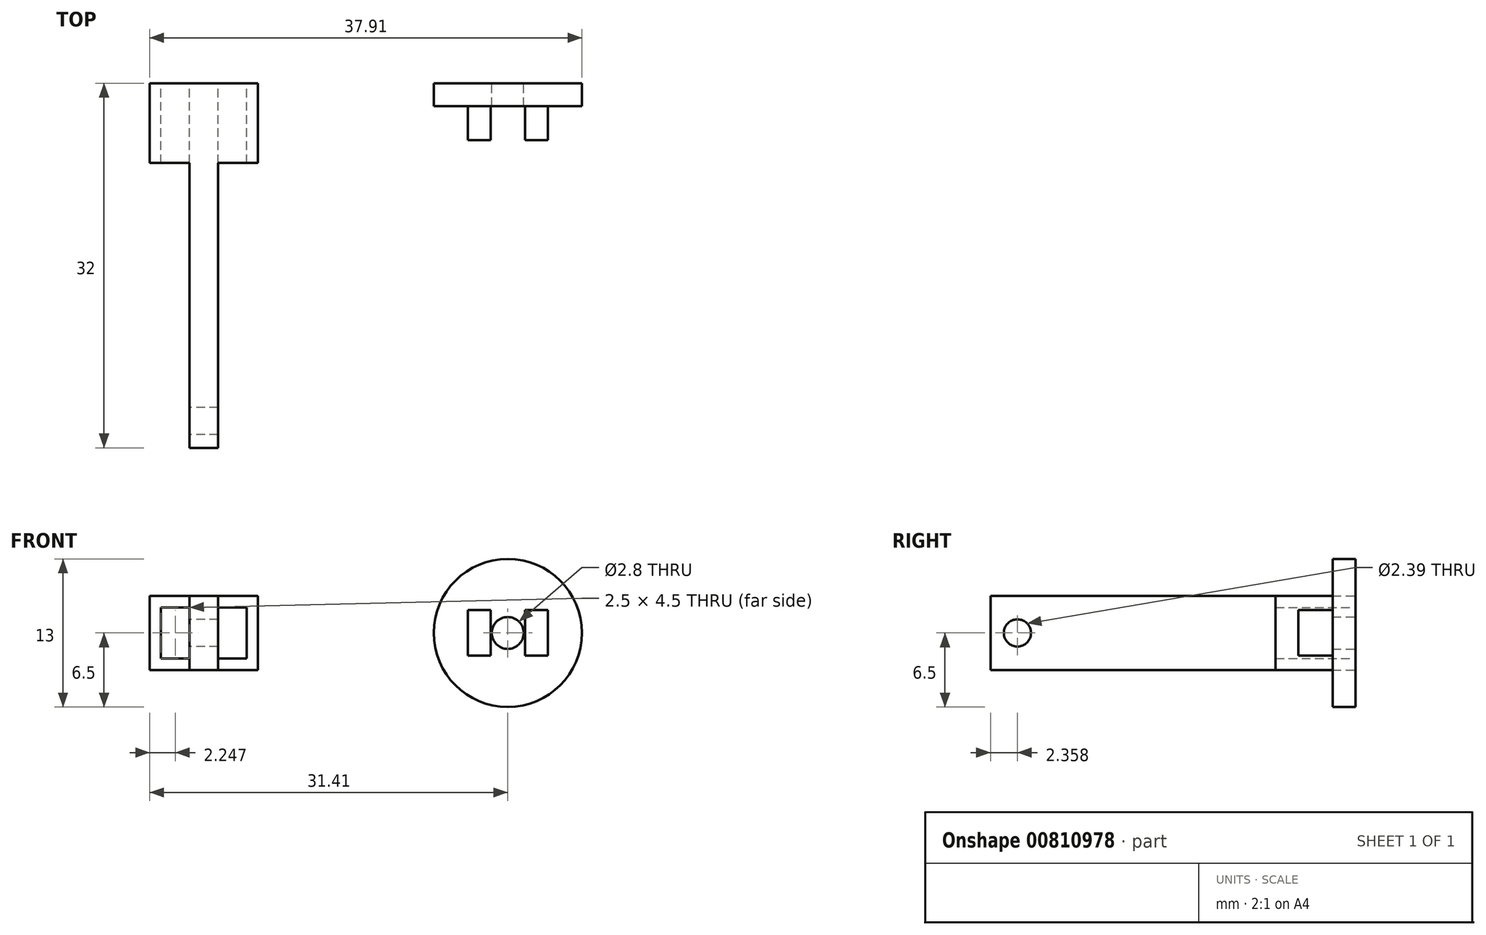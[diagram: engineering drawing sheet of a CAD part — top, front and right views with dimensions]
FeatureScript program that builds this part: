
annotation { "Feature Type Name" : "Feature", "Feature Type Description" : "" }
export const myFeature = defineFeature(function(context is Context, id is Id, definition is map)
    precondition{}
    {
        {
            var Q0;
            Q0=qCreatedBy(makeId("Front.planeOp"),FACE);
            var sketch = newSketch(context, id + "F0", { "sketchPlane" : qUnion([Q0])});
            skCircle(sketch, "E0", {"center": v(0, 0) * mm, "radius": 6.5 * mm});
            skCircle(sketch, "E1", {"center": v(0, 0) * mm, "radius": 1.4 * mm});
            skLineSegment(sketch, "E2.bottom", {"start": v(-3.5, -2) * mm, "end": v(-1.5, -2) * mm});
            skLineSegment(sketch, "E2.top", {"start": v(-3.5, 2) * mm, "end": v(-1.5, 2) * mm});
            skLineSegment(sketch, "E2.left", {"start": v(-3.5, -2) * mm, "end": v(-3.5, 2) * mm});
            skLineSegment(sketch, "E2.right", {"start": v(-1.5, -2) * mm, "end": v(-1.5, 2) * mm});
            skPoint(sketch, "E2.middle", {"position": v(-2.5, 0) * mm});
            skLineSegment(sketch, "E3.bottom", {"start": v(3.5, -2) * mm, "end": v(1.5, -2) * mm});
            skLineSegment(sketch, "E3.top", {"start": v(3.5, 2) * mm, "end": v(1.5, 2) * mm});
            skLineSegment(sketch, "E3.left", {"start": v(3.5, -2) * mm, "end": v(3.5, 2) * mm});
            skLineSegment(sketch, "E3.right", {"start": v(1.5, -2) * mm, "end": v(1.5, 2) * mm});
            skPoint(sketch, "E3.middle", {"position": v(2.5, 0) * mm});
            skLineSegment(sketch, "E4.bottom", {"start": v(-21.91, -3.25) * mm, "end": v(-31.41, -3.25) * mm});
            skLineSegment(sketch, "E4.top", {"start": v(-21.91, 3.25) * mm, "end": v(-31.41, 3.25) * mm});
            skLineSegment(sketch, "E4.left", {"start": v(-21.91, -3.25) * mm, "end": v(-21.91, 3.25) * mm});
            skLineSegment(sketch, "E4.right", {"start": v(-31.41, -3.25) * mm, "end": v(-31.41, 3.25) * mm});
            skPoint(sketch, "E4.middle", {"position": v(-26.66, 0) * mm});
            skLineSegment(sketch, "E5.bottom", {"start": v(-30.41, 2.25) * mm, "end": v(-27.91, 2.25) * mm});
            skLineSegment(sketch, "E5.top", {"start": v(-30.41, -2.25) * mm, "end": v(-27.91, -2.25) * mm});
            skLineSegment(sketch, "E5.left", {"start": v(-30.41, 2.25) * mm, "end": v(-30.41, -2.25) * mm});
            skLineSegment(sketch, "E5.right", {"start": v(-27.91, 2.25) * mm, "end": v(-27.91, -2.25) * mm});
            skPoint(sketch, "E5.middle", {"position": v(-29.16, 0) * mm});
            skLineSegment(sketch, "E6.bottom", {"start": v(-22.91, 2.25) * mm, "end": v(-25.41, 2.25) * mm});
            skLineSegment(sketch, "E6.top", {"start": v(-22.91, -2.25) * mm, "end": v(-25.41, -2.25) * mm});
            skLineSegment(sketch, "E6.left", {"start": v(-22.91, 2.25) * mm, "end": v(-22.91, -2.25) * mm});
            skLineSegment(sketch, "E6.right", {"start": v(-25.41, 2.25) * mm, "end": v(-25.41, -2.25) * mm});
            skPoint(sketch, "E6.middle", {"position": v(-24.16, 0) * mm});
            skPoint(sketch, "E7", {"position": v(-25.41, 0) * mm});
            skSolve(sketch);
        }
        {
            var Q0;
            Q0=makeQuery(id+"F0.imprint","IMPRINT",FACE,{"disambiguationData":[TD([[makeQuery(id+"F0.imprint","IMPRINT",EDGE,{"derivedFrom":sQuery(id+"F0.wireOp",EDGE,"E0")}),1.0]])]});
            extrude(context, id + "F1", {"entities" : qUnion([Q0]), "depth" : 2 * mm, "offsetDistance" : 25 * mm});
        }
        {
            var Q0;
            Q0=makeQuery(id+"F0.imprint","IMPRINT",FACE,{"disambiguationData":[TD([[makeQuery(id+"F0.imprint","IMPRINT",EDGE,{"derivedFrom":sQuery(id+"F0.wireOp",EDGE,"E2.bottom")}),1.0]])]});
            var Q1;
            Q1=makeQuery(id+"F0.imprint","IMPRINT",FACE,{"disambiguationData":[TD([[makeQuery(id+"F0.imprint","IMPRINT",EDGE,{"derivedFrom":sQuery(id+"F0.wireOp",EDGE,"E3.bottom")}),-1.0]])]});
            extrude(context, id + "F2", {"entities" : qUnion([Q0, Q1]), "operationType" : NewBodyOperationType.ADD, "depth" : 5 * mm, "offsetDistance" : 25 * mm});
        }
        {
            var Q0;
            Q0=makeQuery(id+"F0.imprint","IMPRINT",FACE,{"disambiguationData":[TD([[makeQuery(id+"F0.imprint","IMPRINT",EDGE,{"derivedFrom":sQuery(id+"F0.wireOp",EDGE,"E4.bottom")}),-1.0]])]});
            extrude(context, id + "F3", {"entities" : qUnion([Q0]), "depth" : 7 * mm, "offsetDistance" : 25 * mm});
        }
        {
            var Q0;
            Q0=makeQuery(id+"F3.opExtrude","CAP_FACE",FACE,{"disambiguationData":[OSD([sQuery(id+"F0.wireOp",EDGE,"E4.bottom"),sQuery(id+"F0.wireOp",EDGE,"E4.top"),sQuery(id+"F0.wireOp",EDGE,"E4.left"),sQuery(id+"F0.wireOp",EDGE,"E4.right"),sQuery(id+"F0.wireOp",EDGE,"E5.bottom"),sQuery(id+"F0.wireOp",EDGE,"E5.top"),sQuery(id+"F0.wireOp",EDGE,"E5.left"),sQuery(id+"F0.wireOp",EDGE,"E5.right"),sQuery(id+"F0.wireOp",EDGE,"E6.bottom"),sQuery(id+"F0.wireOp",EDGE,"E6.top"),sQuery(id+"F0.wireOp",EDGE,"E6.left"),sQuery(id+"F0.wireOp",EDGE,"E6.right")])],"isStart":false});
            var sketch = newSketch(context, id + "F4", { "sketchPlane" : qUnion([Q0])});
            skLineSegment(sketch, "E8.bottom", {"start": v(-25.41, -3.25) * mm, "end": v(-27.9, -3.25) * mm});
            skLineSegment(sketch, "E8.top", {"start": v(-25.41, 3.25) * mm, "end": v(-27.9, 3.25) * mm});
            skLineSegment(sketch, "E8.left", {"start": v(-25.41, -3.25) * mm, "end": v(-25.41, 3.25) * mm});
            skLineSegment(sketch, "E8.right", {"start": v(-27.9, -3.25) * mm, "end": v(-27.9, 3.25) * mm});
            skPoint(sketch, "E8.middle", {"position": v(-26.66, 0) * mm});
            skSolve(sketch);
        }
        {
            var Q0;
            Q0 = qSketchRegion(id + "F4", true);
            extrude(context, id + "F5", {"entities" : qUnion([Q0]), "operationType" : NewBodyOperationType.ADD, "depth" : 25 * mm, "offsetDistance" : 25 * mm});
        }
        {
            var Q0;
            Q0=makeQuery(id+"F5.opExtrude","SWEPT_FACE",FACE,{"disambiguationData":[OSD([sQuery(id+"F4.wireOp",EDGE,"E8.right")])]});
            var sketch = newSketch(context, id + "F6", { "sketchPlane" : qUnion([Q0])});
            skCircle(sketch, "E9", {"center": v(29.64, 0) * mm, "radius": 1.2 * mm});
            skSolve(sketch);
        }
        {
            var Q0;
            Q0=makeQuery(id+"F6.imprint","IMPRINT",FACE,{"disambiguationData":[TD([[makeQuery(id+"F6.imprint","IMPRINT",EDGE,{"derivedFrom":sQuery(id+"F6.wireOp",EDGE,"E9")}),1.0]])]});
            extrude(context, id + "F7", {"entities" : qUnion([Q0]), "operationType" : NewBodyOperationType.REMOVE, "oppositeDirection" : true, "depth" : 25 * mm, "offsetDistance" : 25 * mm});
        }
    });
